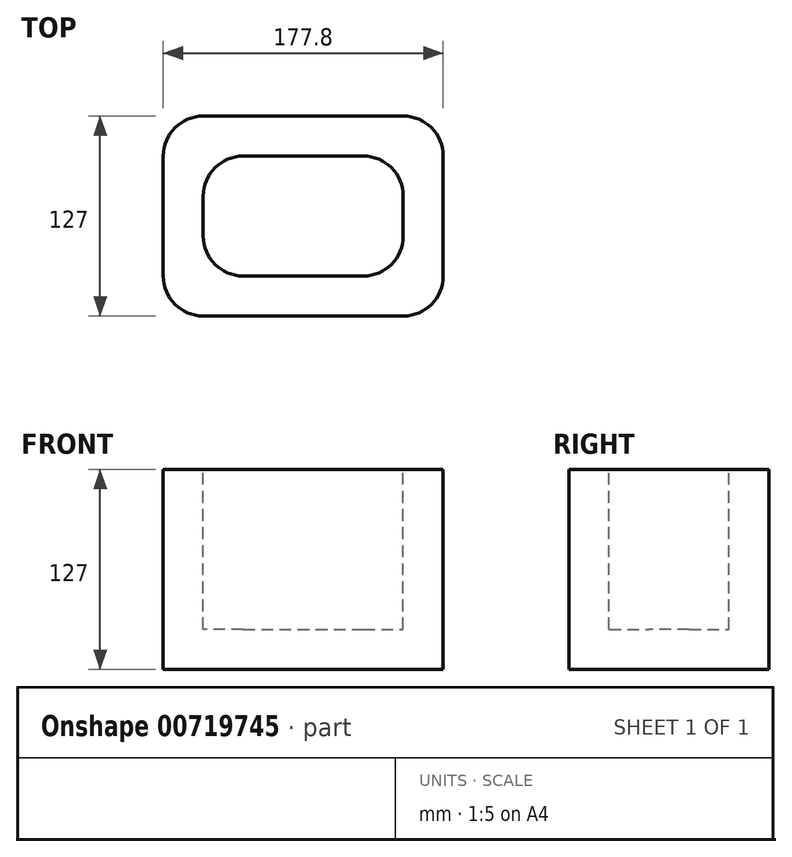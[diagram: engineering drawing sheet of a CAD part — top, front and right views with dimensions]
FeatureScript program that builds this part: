
annotation { "Feature Type Name" : "Feature", "Feature Type Description" : "" }
export const myFeature = defineFeature(function(context is Context, id is Id, definition is map)
    precondition{}
    {
        {
            var Q0;
            Q0=qCreatedBy(makeId("Top.planeOp"),FACE);
            var sketch = newSketch(context, id + "F0", { "sketchPlane" : qUnion([Q0])});
            skLineSegment(sketch, "E0.bottom", {"start": v(0, 0) * mm, "end": v(177.8, 0) * mm});
            skLineSegment(sketch, "E0.top", {"start": v(0, -127) * mm, "end": v(177.8, -127) * mm});
            skLineSegment(sketch, "E0.left", {"start": v(0, 0) * mm, "end": v(0, -127) * mm});
            skLineSegment(sketch, "E0.right", {"start": v(177.8, 0) * mm, "end": v(177.8, -127) * mm});
            skSolve(sketch);
        }
        {
            var Q0;
            Q0 = qSketchRegion(id + "F0", true);
            extrude(context, id + "F1", {"entities" : qUnion([Q0]), "depth" : 127 * mm, "offsetDistance" : 25.4 * mm});
        }
        {
            var Q0;
            Q0=makeQuery(id+"F1.opExtrude","SWEPT_EDGE",EDGE,{"disambiguationData":[OSD([sQuery(id+"F0.wireOp",EDGE,"E0.top"),sQuery(id+"F0.wireOp",EDGE,"E0.left")])]});
            var Q1;
            Q1=makeQuery(id+"F1.opExtrude","SWEPT_EDGE",EDGE,{"disambiguationData":[OSD([sQuery(id+"F0.wireOp",EDGE,"E0.top"),sQuery(id+"F0.wireOp",EDGE,"E0.right")])]});
            var Q2;
            Q2=makeQuery(id+"F1.opExtrude","SWEPT_EDGE",EDGE,{"disambiguationData":[OSD([sQuery(id+"F0.wireOp",EDGE,"E0.bottom"),sQuery(id+"F0.wireOp",EDGE,"E0.right")])]});
            var Q3;
            Q3=makeQuery(id+"F1.opExtrude","SWEPT_EDGE",EDGE,{"disambiguationData":[OSD([sQuery(id+"F0.wireOp",EDGE,"E0.bottom"),sQuery(id+"F0.wireOp",EDGE,"E0.left")])]});
            fillet(context, id + "F2", {"entities" : qUnion([Q0, Q1, Q2, Q3]), "radius" : 25.4 * mm, "tangentPropagation" : true, "allowEdgeOverflow" : false});
        }
        {
            var Q0;
            Q0=makeQuery(id+"F1.opExtrude","CAP_FACE",FACE,{"disambiguationData":[OSD([sQuery(id+"F0.wireOp",EDGE,"E0.bottom"),sQuery(id+"F0.wireOp",EDGE,"E0.top"),sQuery(id+"F0.wireOp",EDGE,"E0.left"),sQuery(id+"F0.wireOp",EDGE,"E0.right")])],"isStart":false});
            shell(context, id + "F3", {"entities" : qUnion([Q0]), "thickness" : 25.4 * mm});
        }
        {
            var Q0;
            Q0=makeQuery(id+"F3.opShell","OFFSET_EDGE",EDGE,{"disambiguationData":[OSD([sQuery(id+"F0.wireOp",EDGE,"E0.bottom"),sQuery(id+"F0.wireOp",EDGE,"E0.left")])]});
            var Q1;
            Q1=makeQuery(id+"F3.opShell","OFFSET_EDGE",EDGE,{"disambiguationData":[OSD([sQuery(id+"F0.wireOp",EDGE,"E0.bottom"),sQuery(id+"F0.wireOp",EDGE,"E0.right")])]});
            var Q2;
            Q2=makeQuery(id+"F3.opShell","OFFSET_EDGE",EDGE,{"disambiguationData":[OSD([sQuery(id+"F0.wireOp",EDGE,"E0.top"),sQuery(id+"F0.wireOp",EDGE,"E0.left")])]});
            var Q3;
            Q3=makeQuery(id+"F3.opShell","OFFSET_EDGE",EDGE,{"disambiguationData":[OSD([sQuery(id+"F0.wireOp",EDGE,"E0.top"),sQuery(id+"F0.wireOp",EDGE,"E0.right")])]});
            fillet(context, id + "F4", {"entities" : qUnion([Q0, Q1, Q2, Q3]), "radius" : 25.4 * mm, "tangentPropagation" : true, "allowEdgeOverflow" : false});
        }
    });
